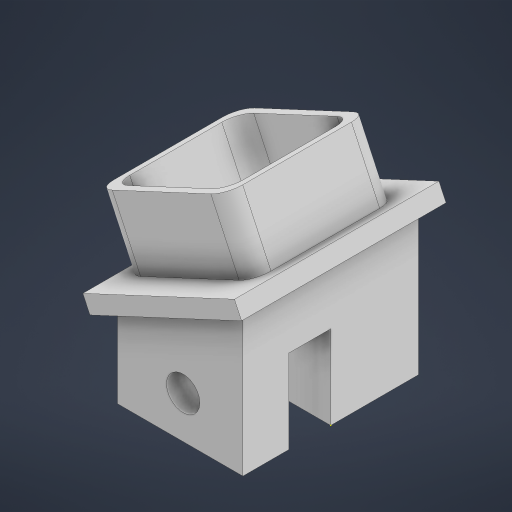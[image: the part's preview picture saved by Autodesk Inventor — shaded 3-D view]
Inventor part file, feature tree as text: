
AUTODESK INVENTOR PART (.ipt)
format: ipt  version: 2024 (Build 280153000, 153)  size: 257,536 bytes
history: native  units: mm
features: reference x11, sketch x6, extrude x5, other x4, fillet x1, projected_geometry x1
ambient origin geometry x8: Origin, YZ Plane, XZ Plane, XY Plane, X Axis, Y Axis, Z Axis, Center Point
bodies: Body1 (feature_tree)
feature tree (28):
  other  "Твердое тело1"
  extrude  "Выдавливание1"  Depth=10.0mm TaperAngle=0.0deg
  extrude  "Выдавливание2"  Depth=10.0mm TaperAngle=0.0deg
  extrude  "Выдавливание3"  Depth=4.363323mm
  extrude  "Выдавливание4"  Depth=10.0mm TaperAngle=0.0deg
  extrude  "Выдавливание5"  Depth=20.0mm
  fillet  "Сопряжение1"  Radius=2.0mm
  sketch  "Эскиз6"
  sketch  "Эскиз1"
  reference  "Ссылка1"
  reference  "Ссылка2"
  reference  "Ссылка3"
  reference  "Ссылка4"
  reference  "Ссылка5"
  reference  "Ссылка6"
  reference  "Ссылка7"
  reference  "Ссылка8"
  reference  "Ссылка16"
  reference  "Ссылка17"
  sketch  "Эскиз2"
  reference  "Ссылка18"
  sketch  "Эскиз3"
  sketch  "Эскиз4"
  projected_geometry  "Спроецированная петля1"
  sketch  "Эскиз5"
  parser-record x1  (decoder bookkeeping rows leaked as tree rows — omitted from the tree; the rows remain in map.json)
  other  "cum_holder_asembly.iam"
  other  "cum_holder_up:1"
note: 1 file-system path scrubbed to <path> (originals preserved in map.json)
